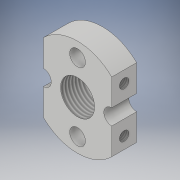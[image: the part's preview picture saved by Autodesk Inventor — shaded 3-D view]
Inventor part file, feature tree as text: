
AUTODESK INVENTOR PART (.ipt)
format: ipt  version: 2019.1 (Build 231200000, 200)  size: 151,552 bytes
history: native  units: in
note: dims shown in document units (in); Inventor stores cm internally (conversion verified against a paired STEP export)
features: sketch x4, extrude x2, hole x2, thread x1, pattern_circular x1, mirror x1, projected_geometry x1
ambient origin geometry x8: Origin, YZ Plane, XZ Plane, XY Plane, X Axis, Y Axis, Z Axis, Center Point
bodies: Solid1 (feature_tree)
feature tree (12):
  extrude  "Extrusion1"  Depth=0.41in
  thread  "Thread1"  [1 undecoded]
  hole  "Hole1"  [1 undecoded]
  pattern_circular  "Circular Pattern1"  Count=4 Angle=360.0deg
  extrude  "Extrusion2"  Depth=0.41in
  hole  "Hole2"  [1 undecoded]
  mirror  "Mirror1"
  sketch  "Sketch1"  dims[d0=0.5625in d1=1.6in d2=0.41in d3=0.0in]
  sketch  "Sketch2"  dims[d4=1.0in d5=0.0in d6=0.5625in]
  sketch  "Sketch3"  dims[d7=0.26in d8=0.328in d9=0.375in d10=0.25in d11=0.5635in d12=0.484in d13=0.8108in d14=1.5748in d15=360.0deg]
  sketch  "Sketch4"  dims[d17=1.125in d18=0.5625in d19=0.41in d20=0.0in d21=0.375in d22=0.375in d23=0.156in d24=0.38in d25=0.375in d26=0.25in d27=0.5635in d28=0.45in d29=0.8108in]
  projected_geometry  "Projected Loop1"
note: 3 required parameter values undecoded (feature->parameter linkage not recoverable at this tier; creation-order binding heuristic only, values carry confidence <= 0.55)
